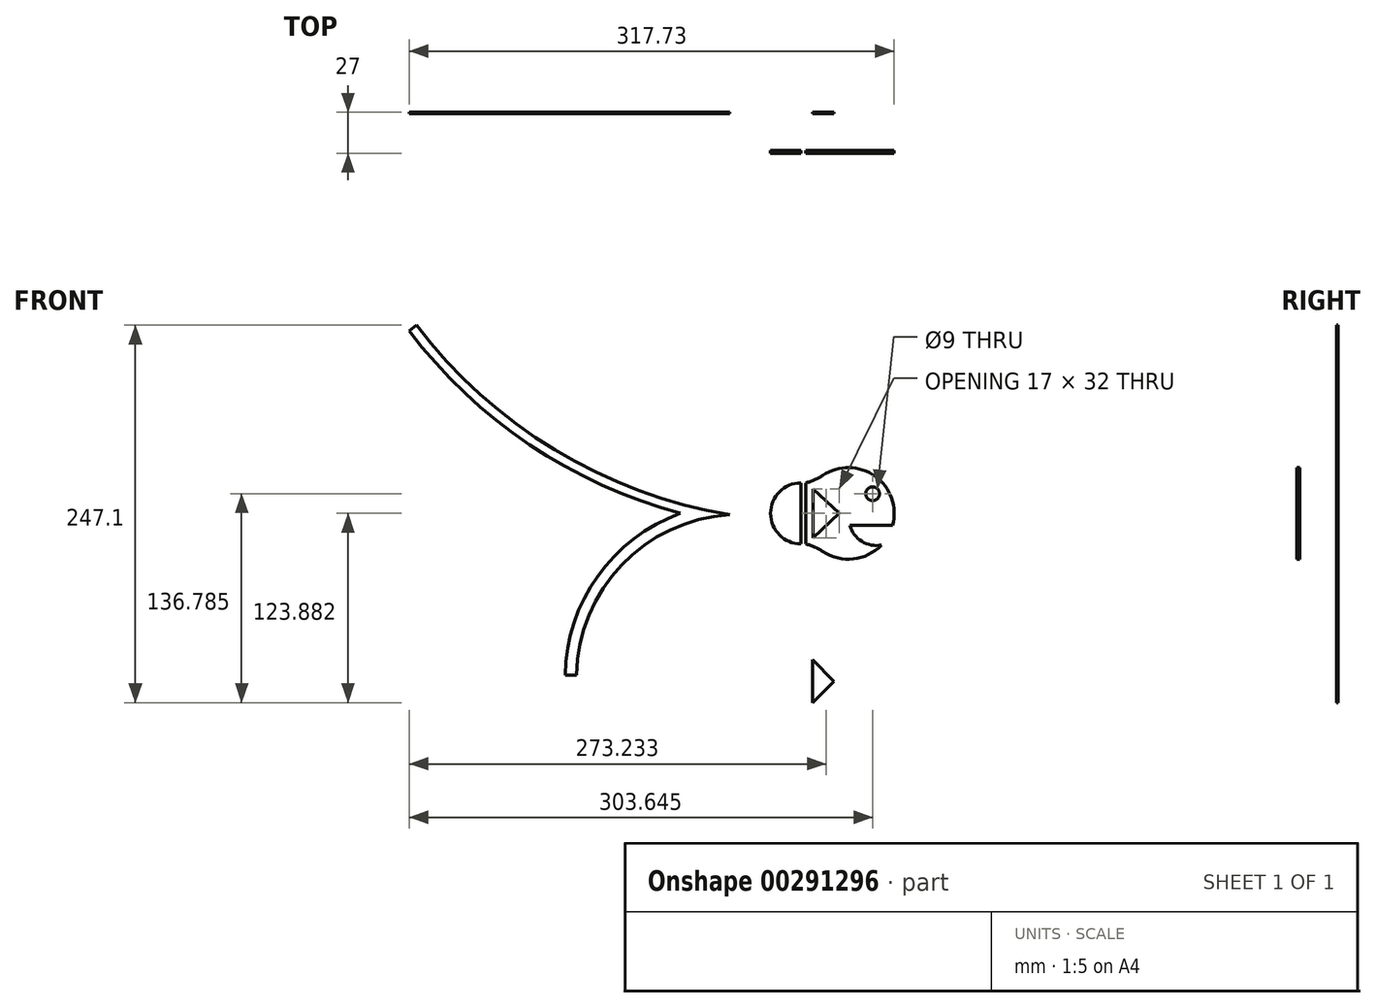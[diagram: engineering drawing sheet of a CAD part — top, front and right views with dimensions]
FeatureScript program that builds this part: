
annotation { "Feature Type Name" : "Feature", "Feature Type Description" : "" }
export const myFeature = defineFeature(function(context is Context, id is Id, definition is map)
    precondition{}
    {
        {
            var Q0;
            Q0=qCreatedBy(makeId("Front.planeOp"),FACE);
            var sketch = newSketch(context, id + "F0", { "sketchPlane" : qUnion([Q0])});
            skCircle(sketch, "E0", {"center": v(0, 0) * mm, "radius": 25.5 * mm});
            skLineSegment(sketch, "E1", {"start": v(0, 0) * mm, "end": v(-10, 0) * mm});
            skLineSegment(sketch, "E2", {"start": v(-10, 0) * mm, "end": v(-10, -25.5) * mm});
            skLineSegment(sketch, "E3", {"start": v(0, 0) * mm, "end": v(10, 0) * mm});
            skLineSegment(sketch, "E4", {"start": v(10, 0) * mm, "end": v(10, -25.5) * mm});
            skCircle(sketch, "E5", {"center": v(-7.44, 13.61) * mm, "radius": 2.56 * mm});
            skLineSegment(sketch, "E6", {"start": v(-73.6, -50.22) * mm, "end": v(-107.76, -50.22) * mm});
            skArc(sketch, "E7", {"start": v(-15, -25.5) * mm, "mid": v(-17.75, -19.78) * mm, "end": v(-21.06, -14.37) * mm});
            skArc(sketch, "E8.MirrorCS", {"start": v(15, -25.5) * mm, "mid": v(17.75, -19.78) * mm, "end": v(21.06, -14.37) * mm});
            skCircle(sketch, "E9", {"center": v(113.72, 0) * mm, "radius": 25 * mm});
            skLineSegment(sketch, "E10", {"start": v(138.72, 0) * mm, "end": v(138.72, -50) * mm});
            skLineSegment(sketch, "E11", {"start": v(113.72, -25) * mm, "end": v(163.72, -25) * mm});
            skLineSegment(sketch, "E12", {"start": v(163.72, -25) * mm, "end": v(138.72, -50) * mm});
            skPoint(sketch, "E13.orphan", {"position": v(213.72, -25) * mm});
            skPoint(sketch, "E14.orphan", {"position": v(138.72, -100) * mm});
            skCircle(sketch, "E15", {"center": v(123.47, 14.02) * mm, "radius": 4.35 * mm});
            skLineSegment(sketch, "E16", {"start": v(91.04, 10.52) * mm, "end": v(105.58, -3.87) * mm});
            skCircle(sketch, "E17", {"center": v(-226.65, -33.63) * mm, "radius": 25 * mm});
            skLineSegment(sketch, "E18", {"start": v(-226.65, -33.63) * mm, "end": v(-244.82, -50.8) * mm});
            skLineSegment(sketch, "E19", {"start": v(-244.82, -50.8) * mm, "end": v(-199.98, -98.23) * mm});
            skLineSegment(sketch, "E20", {"start": v(-226.65, -33.63) * mm, "end": v(-206.74, -48.74) * mm});
            skLineSegment(sketch, "E21", {"start": v(-206.74, -48.74) * mm, "end": v(-244.3, -98.23) * mm});
            skLineSegment(sketch, "E22", {"start": v(-199.98, -98.23) * mm, "end": v(-244.3, -98.23) * mm});
            skLineSegment(sketch, "E23", {"start": v(0, -25.5) * mm, "end": v(-10, -25.5) * mm});
            skPoint(sketch, "E23.endSnap0", {"position": v(-15.76, -23.78) * mm});
            skLineSegment(sketch, "E24", {"start": v(0, -25.5) * mm, "end": v(15, -25.5) * mm});
            skPoint(sketch, "E25.orphan", {"position": v(10, -50.22) * mm});
            skPoint(sketch, "E26.orphan", {"position": v(-10, -50.22) * mm});
            skPoint(sketch, "E27.orphan", {"position": v(-15.76, -25.5) * mm});
            skLineSegment(sketch, "E28", {"start": v(-10, -25.5) * mm, "end": v(-15, -25.5) * mm});
            skLineSegment(sketch, "E29", {"start": v(0, -25.5) * mm, "end": v(0, -27.32) * mm});
            skLineSegment(sketch, "E30", {"start": v(0, -27.32) * mm, "end": v(-15, -27.32) * mm});
            skLineSegment(sketch, "E31", {"start": v(-15, -27.32) * mm, "end": v(15, -27.32) * mm});
            skPoint(sketch, "E32", {"position": v(0, -43.36) * mm});
            skArc(sketch, "E33", {"start": v(-15, -27.32) * mm, "mid": v(0, -43.36) * mm, "end": v(15, -27.32) * mm});
            skLineSegment(sketch, "E34", {"start": v(0, 38.83) * mm, "end": v(3.29, 38.83) * mm});
            skLineSegment(sketch, "E35", {"start": v(3.29, 38.83) * mm, "end": v(3.29, 60.8) * mm});
            skLineSegment(sketch, "E36", {"start": v(3.29, 60.8) * mm, "end": v(-3.32, 60.8) * mm});
            skLineSegment(sketch, "E37", {"start": v(-3.32, 60.8) * mm, "end": v(-3.32, 38.83) * mm});
            skLineSegment(sketch, "E38", {"start": v(-3.32, 38.83) * mm, "end": v(0, 38.83) * mm});
            skLineSegment(sketch, "E39", {"start": v(0, 0) * mm, "end": v(0, 4.38) * mm});
            skLineSegment(sketch, "E40", {"start": v(0, 4.38) * mm, "end": v(9, 4.38) * mm});
            skLineSegment(sketch, "E41", {"start": v(9, 4.38) * mm, "end": v(9, 23.86) * mm});
            skLineSegment(sketch, "E42", {"start": v(9, 18.38) * mm, "end": v(17.68, 18.38) * mm});
            skArc(sketch, "E43", {"start": v(9, 4.38) * mm, "mid": v(15.04, 10.32) * mm, "end": v(17.68, 18.38) * mm});
            skSolve(sketch);
        }
        {
            var Q0;
            Q0=qCreatedBy(makeId("Front.planeOp"),FACE);
            cPlane(context, id + "F1", {"entities" : qUnion([Q0]), "cplaneType" : CPlaneType.OFFSET, "offset" : 25 * mm, "width" : 150 * mm, "height" : 150 * mm});
        }
        {
            var Q0;
            Q0=qCreatedBy(makeId("Right.planeOp"),FACE);
            var sketch = newSketch(context, id + "F2", { "sketchPlane" : qUnion([Q0])});
            skArc(sketch, "E44", {"start": v(15.7, -19.46) * mm, "mid": v(0, 25) * mm, "end": v(-15.7, -19.46) * mm});
            skLineSegment(sketch, "E45", {"start": v(0, 0) * mm, "end": v(0, -23) * mm});
            skLineSegment(sketch, "E46", {"start": v(-14, -23) * mm, "end": v(14, -23) * mm});
            skLineSegment(sketch, "E47", {"start": v(-14, -25) * mm, "end": v(-14, -51.36) * mm});
            skArc(sketch, "E48", {"start": v(-14, -23) * mm, "mid": v(-14.44, -21.04) * mm, "end": v(-15.7, -19.46) * mm});
            skLineSegment(sketch, "E49", {"start": v(14, -25) * mm, "end": v(14, -49.5) * mm});
            skArc(sketch, "E50.MirrorCS", {"start": v(14, -23) * mm, "mid": v(14.44, -21.04) * mm, "end": v(15.7, -19.46) * mm});
            skLineSegment(sketch, "E51", {"start": v(0, -23) * mm, "end": v(0, -25) * mm});
            skLineSegment(sketch, "E52", {"start": v(-14, -25) * mm, "end": v(14, -25) * mm});
            skPoint(sketch, "E53", {"position": v(0, -39) * mm});
            skArc(sketch, "E54", {"start": v(-14, -25) * mm, "mid": v(0, -39) * mm, "end": v(14, -25) * mm});
            skLineSegment(sketch, "E55", {"start": v(0, 0) * mm, "end": v(-24.92, 0) * mm});
            skLineSegment(sketch, "E56", {"start": v(-24.92, 0) * mm, "end": v(-24.92, 2) * mm});
            skLineSegment(sketch, "E57", {"start": v(-24.92, 2) * mm, "end": v(-13.16, 2) * mm});
            skLineSegment(sketch, "E58", {"start": v(-13.16, 2) * mm, "end": v(0.84, 2) * mm});
            skLineSegment(sketch, "E59", {"start": v(0.84, 2) * mm, "end": v(10.4, 2) * mm});
            skArc(sketch, "E60", {"start": v(0.84, 2) * mm, "mid": v(-6.16, 4.61) * mm, "end": v(-13.16, 2) * mm});
            skArc(sketch, "E61", {"start": v(0.84, 2) * mm, "mid": v(5.3, -0.62) * mm, "end": v(10.4, -1.45) * mm});
            skArc(sketch, "E62.MirrorCS", {"start": v(0.84, 2) * mm, "mid": v(-6.16, -0.61) * mm, "end": v(-13.16, 2) * mm});
            skArc(sketch, "E63.MirrorCS", {"start": v(0.84, 2) * mm, "mid": v(5.3, 4.62) * mm, "end": v(10.4, 5.45) * mm});
            skEllipticalArc(sketch, "E64", {});
            const initialGuessF2  = {"E64": [0.010409135939553385, 0.002, 0, 1, 0.0034459121739491803, 0.004970570865805581, 6.283185307179586, 3.141592653589793]};
            skSetInitialGuess(sketch, initialGuessF2);
            skSolve(sketch);
        }
        {
            var Q0;
            Q0=qCreatedBy(makeId("Right.planeOp"),FACE);
            cPlane(context, id + "F3", {"entities" : qUnion([Q0]), "cplaneType" : CPlaneType.OFFSET, "offset" : 25 * mm, "width" : 150 * mm, "height" : 150 * mm});
        }
        {
            var Q0;
            Q0=qCreatedBy(makeId("Front.planeOp"),FACE);
            var sketch = newSketch(context, id + "F4", { "sketchPlane" : qUnion([Q0])});
            skCircle(sketch, "E65", {"center": v(-370.47, -19.3) * mm, "radius": 30 * mm});
            skCircle(sketch, "E66", {"center": v(-354.55, -6.4) * mm, "radius": 4.5 * mm});
            skLineSegment(sketch, "E67", {"start": v(-341.53, -27.23) * mm, "end": v(-369.53, -27.23) * mm});
            skLineSegment(sketch, "E68", {"start": v(-348.78, -27.23) * mm, "end": v(-348.78, -40.04) * mm});
            skArc(sketch, "E69", {"start": v(-369.53, -27.23) * mm, "mid": v(-361.6, -37.6) * mm, "end": v(-348.78, -40.04) * mm});
            skArc(sketch, "E70", {"start": v(-326.76, 5.18) * mm, "mid": v(-338.58, 7.71) * mm, "end": v(-346.2, -1.67) * mm});
            skLineSegment(sketch, "E71", {"start": v(-398.47, 0.66) * mm, "end": v(-398.47, -39.28) * mm});
            skPoint(sketch, "E72", {"position": v(-398.47, -19.3) * mm});
            skArc(sketch, "E73", {"start": v(-398.47, 0.66) * mm, "mid": v(-392.6, 2.62) * mm, "end": v(-387.2, 5.6) * mm});
            skLineSegment(sketch, "E74", {"start": v(-370.47, -19.3) * mm, "end": v(-398.47, -19.3) * mm});
            skArc(sketch, "E75.MirrorCS", {"start": v(-398.47, -39.28) * mm, "mid": v(-392.6, -41.24) * mm, "end": v(-387.2, -44.21) * mm});
            skLineSegment(sketch, "E76", {"start": v(-401.47, 0.66) * mm, "end": v(-401.47, -39.28) * mm});
            skArc(sketch, "E77", {"start": v(-401.47, -39.28) * mm, "mid": v(-421.44, -19.3) * mm, "end": v(-401.47, 0.66) * mm});
            skLineSegment(sketch, "E78", {"start": v(-326.76, 5.18) * mm, "end": v(-316.43, -4.66) * mm});
            skArc(sketch, "E79", {"start": v(-321.62, 5.09) * mm, "mid": v(-326.76, 5.18) * mm, "end": v(-326.43, 0.04) * mm});
            skCircle(sketch, "E80", {"center": v(-320.28, -1) * mm, "radius": 5 * mm});
            skArc(sketch, "E81", {"start": v(-321.25, 4.74) * mm, "mid": v(-320.3, 4.22) * mm, "end": v(-319.26, 3.9) * mm});
            skArc(sketch, "E82.MirrorCS", {"start": v(-326.06, -0.3) * mm, "mid": v(-325.5, -1.24) * mm, "end": v(-325.12, -2.26) * mm});
            skLineSegment(sketch, "E83", {"start": v(-316.66, -4.44) * mm, "end": v(-318.04, -3.13) * mm});
            skLineSegment(sketch, "E84", {"start": v(-318.04, -3.13) * mm, "end": v(-316.78, -1.81) * mm});
            skCircle(sketch, "E85", {"center": v(-316.78, -1.81) * mm, "radius": 0.72 * mm});
            skLineSegment(sketch, "E86", {"start": v(-318.5, -5.67) * mm, "end": v(-320.28, -3.98) * mm});
            skLineSegment(sketch, "E87", {"start": v(-319.05, -5.15) * mm, "end": v(-319.84, -5.98) * mm});
            skArc(sketch, "E88", {"start": v(-320.28, -3.98) * mm, "mid": v(-320.39, -5.05) * mm, "end": v(-319.84, -5.98) * mm});
            skLineSegment(sketch, "E89", {"start": v(-321.25, 4.74) * mm, "end": v(-326.06, -0.3) * mm});
            skLineSegment(sketch, "E90", {"start": v(-321.62, 5.09) * mm, "end": v(-326.43, 0.04) * mm});
            skLineSegment(sketch, "E91", {"start": v(-376.47, -19.3) * mm, "end": v(-393.47, -3.3) * mm});
            skLineSegment(sketch, "E92", {"start": v(-393.47, -3.3) * mm, "end": v(-393.47, -19.3) * mm});
            skLineSegment(sketch, "E93.MirrorCS", {"start": v(-376.47, -19.3) * mm, "end": v(-393.47, -35.3) * mm});
            skLineSegment(sketch, "E94.MirrorCS", {"start": v(-393.47, -35.3) * mm, "end": v(-393.47, -19.3) * mm});
            skSolve(sketch);
        }
        {
            var Q0;
            Q0=qCreatedBy(id+"F1.planeOp",FACE);
            var sketch = newSketch(context, id + "F5", { "sketchPlane" : qUnion([Q0])});
            skArc(sketch, "E95.0", {"start": v(-387.2, -44.21) * mm, "mid": v(-367.23, -49.13) * mm, "end": v(-348.78, -40.04) * mm});
            skArc(sketch, "E96.0", {"start": v(-398.47, 0.66) * mm, "mid": v(-392.6, 2.62) * mm, "end": v(-387.2, 5.6) * mm});
            skArc(sketch, "E97.0", {"start": v(-398.47, -39.28) * mm, "mid": v(-392.6, -41.24) * mm, "end": v(-387.2, -44.21) * mm});
            skLineSegment(sketch, "E98.0", {"start": v(-398.47, 0.66) * mm, "end": v(-398.47, -39.28) * mm});
            skLineSegment(sketch, "E99.0", {"start": v(-341.53, -27.23) * mm, "end": v(-369.53, -27.23) * mm});
            skArc(sketch, "E100.0", {"start": v(-369.53, -27.23) * mm, "mid": v(-361.6, -37.6) * mm, "end": v(-348.78, -40.04) * mm});
            skLineSegment(sketch, "E101.0", {"start": v(-376.47, -19.3) * mm, "end": v(-393.47, -35.3) * mm});
            skLineSegment(sketch, "E102.0", {"start": v(-393.47, -3.3) * mm, "end": v(-393.47, -19.3) * mm});
            skLineSegment(sketch, "E103.0", {"start": v(-393.47, -35.3) * mm, "end": v(-393.47, -19.3) * mm});
            skLineSegment(sketch, "E104.0", {"start": v(-376.47, -19.3) * mm, "end": v(-393.47, -3.3) * mm});
            skLineSegment(sketch, "E105.0", {"start": v(-401.47, 0.66) * mm, "end": v(-401.47, -39.28) * mm});
            skArc(sketch, "E106.0", {"start": v(-401.47, -39.28) * mm, "mid": v(-421.44, -19.3) * mm, "end": v(-401.47, 0.66) * mm});
            skArc(sketch, "E107.trimOffspring", {"start": v(-341.53, -27.23) * mm, "mid": v(-352.95, 5.05) * mm, "end": v(-387.2, 5.6) * mm});
            skCircle(sketch, "E108.0", {"center": v(-354.55, -6.4) * mm, "radius": 4.5 * mm});
            skSolve(sketch);
        }
        {
            var Q0;
            Q0 = qSketchRegion(id + "F5", true);
            var Q1;
            Q1=makeQuery(id+"F5.imprint","IMPRINT",FACE,{"disambiguationData":[TD([[makeQuery(id+"F5.imprint","IMPRINT",EDGE,{"derivedFrom":sQuery(id+"F5.wireOp",EDGE,"Z9ecCXPI-NCrY-evfy-3BdF-ezJmGdb5R1DG")}),1.0]])]});
            extrude(context, id + "F6", {"entities" : qUnion([Q0, Q1]), "depth" : 2 * mm, "offsetDistance" : 25 * mm});
        }
        {
            var Q0;
            Q0=qCreatedBy(makeId("Front.planeOp"),FACE);
            var sketch = newSketch(context, id + "F7", { "sketchPlane" : qUnion([Q0])});
            skArc(sketch, "E109.0", {"start": v(-341.53, -27.23) * mm, "mid": v(-352.95, 5.05) * mm, "end": v(-387.2, 5.6) * mm});
            skArc(sketch, "E110.0", {"start": v(-401.47, -39.28) * mm, "mid": v(-421.44, -19.3) * mm, "end": v(-401.47, 0.66) * mm});
            skLineSegment(sketch, "E111", {"start": v(-370.47, -19.3) * mm, "end": v(-551.17, -19.3) * mm, "construction": true});
            skPoint(sketch, "E111.endSnap0", {"position": v(-421.44, -19.3) * mm});
            skPoint(sketch, "E112", {"position": v(-480.47, -19.3) * mm});
            skPoint(sketch, "E113.second.point", {"position": v(-563.57, 539.34) * mm});
            skPoint(sketch, "E113.third.point", {"position": v(-669.78, 357.26) * mm});
            skPoint(sketch, "E114.second.point", {"position": v(-466, -215.64) * mm});
            skPoint(sketch, "E114.third.point", {"position": v(-366, -235.94) * mm});
            skArc(sketch, "E115", {"start": v(-658.2, 100.28) * mm, "mid": v(-579.26, 25.74) * mm, "end": v(-480.47, -19.3) * mm});
            skArc(sketch, "E116", {"start": v(-480.47, -19.3) * mm, "mid": v(-534.7, -60.44) * mm, "end": v(-555.94, -125.1) * mm});
            skLineSegment(sketch, "E117", {"start": v(-658.2, 100.28) * mm, "end": v(-653.42, 103.91) * mm});
            skPoint(sketch, "E118", {"position": v(-653.42, 103.91) * mm});
            skLineSegment(sketch, "E119", {"start": v(-548.44, -125.22) * mm, "end": v(-555.94, -125.1) * mm});
            skPoint(sketch, "E120", {"position": v(-548.44, -125.22) * mm});
            skPoint(sketch, "E121", {"position": v(-548.45, -125.76) * mm});
            skPoint(sketch, "E122", {"position": v(-519.06, -53.23) * mm});
            skArc(sketch, "E123", {"start": v(-448.27, -20.21) * mm, "mid": v(-518.93, -53.09) * mm, "end": v(-548.44, -125.22) * mm});
            skPoint(sketch, "E124", {"position": v(-543.37, 11.47) * mm});
            skArc(sketch, "E125", {"start": v(-653.42, 103.91) * mm, "mid": v(-562.68, 22.28) * mm, "end": v(-448.27, -20.21) * mm});
            skPoint(sketch, "E126", {"position": v(-391.83, -19.3) * mm});
            skLineSegment(sketch, "E127", {"start": v(-391.83, -19.3) * mm, "end": v(-391.83, -6.8) * mm});
            skLineSegment(sketch, "E128.MirrorCS", {"start": v(-391.83, -19.3) * mm, "end": v(-391.83, -31.83) * mm});
            skLineSegment(sketch, "E129", {"start": v(-393.83, -115.2) * mm, "end": v(-393.83, -143.2) * mm});
            skPoint(sketch, "E130", {"position": v(-393.83, -129.2) * mm});
            skLineSegment(sketch, "E131", {"start": v(-393.83, -143.2) * mm, "end": v(-379.83, -129.2) * mm});
            skLineSegment(sketch, "E132", {"start": v(-379.83, -129.2) * mm, "end": v(-393.83, -115.2) * mm});
            skSolve(sketch);
        }
        {
            var Q0;
            Q0=makeQuery(id+"F7.imprint","IMPRINT",FACE,{"disambiguationData":[TD([[makeQuery(id+"F7.imprint","IMPRINT",EDGE,{"derivedFrom":sQuery(id+"F7.wireOp",EDGE,"E115")}),1.0]])]});
            extrude(context, id + "F8", {"entities" : qUnion([Q0]), "depth" : 1 * mm});
        }
        {
            var Q0;
            Q0 = qSketchRegion(id + "F7", true);
            extrude(context, id + "F9", {"entities" : qUnion([Q0]), "operationType" : NewBodyOperationType.ADD, "depth" : 1 * mm});
        }
    });
